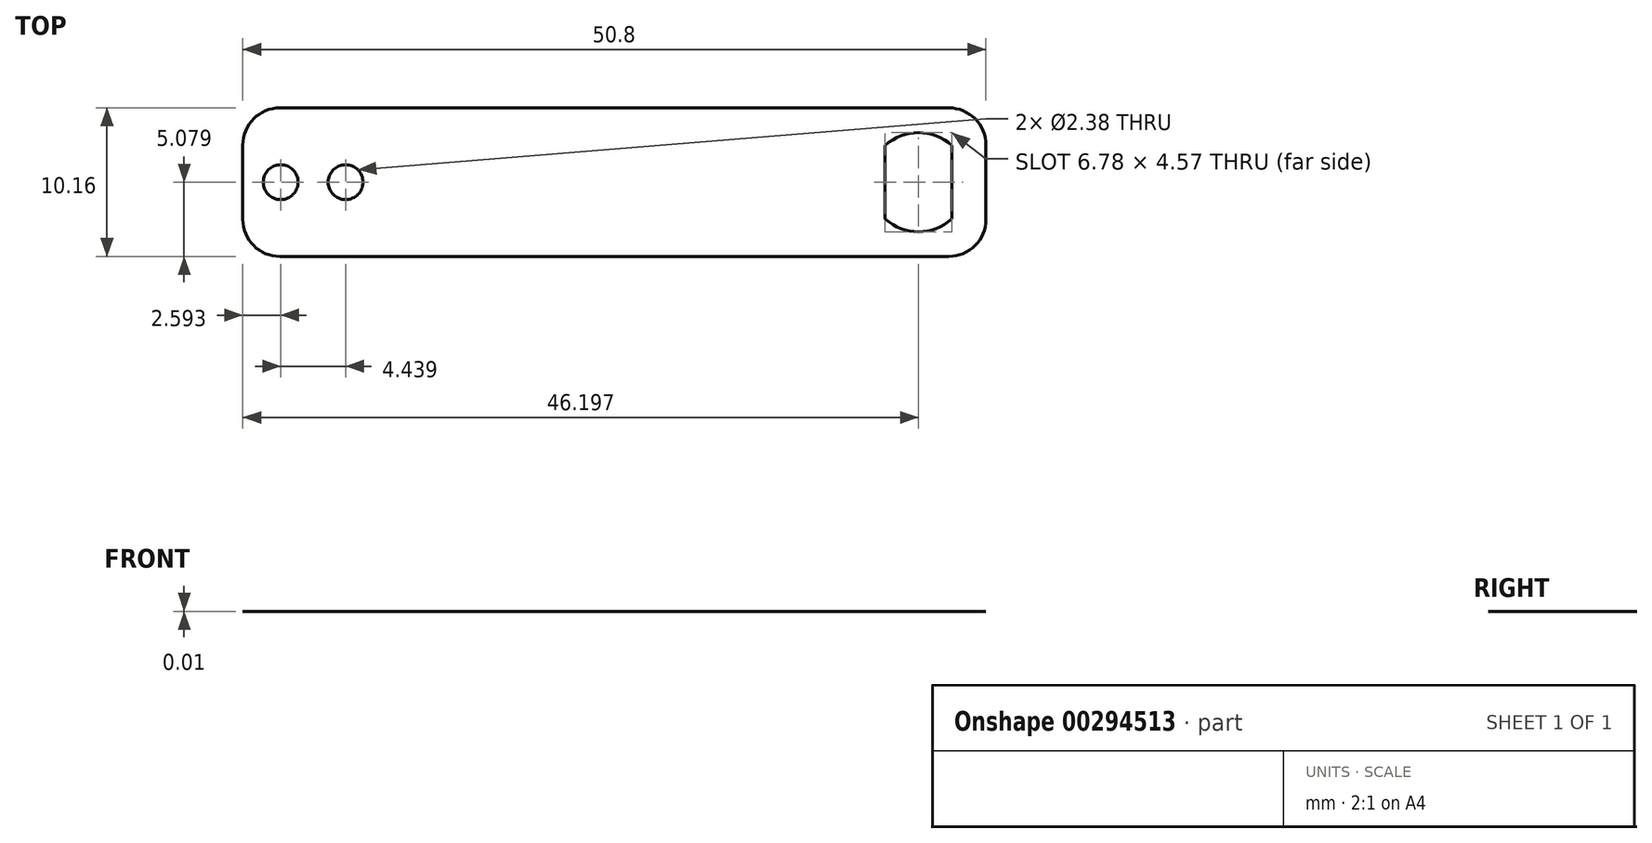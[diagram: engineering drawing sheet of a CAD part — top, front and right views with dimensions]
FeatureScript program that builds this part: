
annotation { "Feature Type Name" : "Feature", "Feature Type Description" : "" }
export const myFeature = defineFeature(function(context is Context, id is Id, definition is map)
    precondition{}
    {
        {
            var Q0;
            Q0=qCreatedBy(makeId("Top.planeOp"),FACE);
            var sketch = newSketch(context, id + "F0", { "sketchPlane" : qUnion([Q0])});
            skLineSegment(sketch, "E0.bottom", {"start": v(23.47, 15.87) * mm, "end": v(-27.33, 15.87) * mm});
            skLineSegment(sketch, "E0.top", {"start": v(23.47, 5.7) * mm, "end": v(-27.33, 5.7) * mm});
            skLineSegment(sketch, "E0.left", {"start": v(23.47, 15.87) * mm, "end": v(23.47, 5.7) * mm});
            skLineSegment(sketch, "E0.right", {"start": v(-27.33, 15.87) * mm, "end": v(-27.33, 5.7) * mm});
            skPoint(sketch, "E0.middle", {"position": v(-1.93, 10.79) * mm});
            skLineSegment(sketch, "E1", {"start": v(-27.33, 10.79) * mm, "end": v(23.47, 10.79) * mm});
            skCircle(sketch, "E2", {"center": v(-24.74, 10.79) * mm, "radius": 1.2 * mm});
            skCircle(sketch, "E3", {"center": v(-20.3, 10.79) * mm, "radius": 1.2 * mm});
            skCircle(sketch, "E4", {"center": v(18.87, 10.79) * mm, "radius": 3.4 * mm});
            skLineSegment(sketch, "E5", {"start": v(16.58, 13.3) * mm, "end": v(16.58, 8.28) * mm});
            skLineSegment(sketch, "E6", {"start": v(21.15, 13.3) * mm, "end": v(21.15, 8.28) * mm});
            skSolve(sketch);
        }
        {
            var Q0;
            {var subQ12=sQuery(id+"F0.wireOp",EDGE,"E0.bottom");Q0=makeQuery(id+"F0.imprint","IMPRINT",FACE,{"disambiguationData":[TD([[makeQuery(id+"F0.imprint","IMPRINT",EDGE,{"derivedFrom":subQ12}),1.0]])]});}
            var Q1;
            {var subQ9=sQuery(id+"F0.wireOp",EDGE,"E0.top");Q1=makeQuery(id+"F0.imprint","IMPRINT",FACE,{"disambiguationData":[TD([[makeQuery(id+"F0.imprint","IMPRINT",EDGE,{"derivedFrom":subQ9}),-1.0]])]});}
            var Q2;
            {var subQ0=sQuery(id+"F0.wireOp",EDGE,"E4");var subQ1=sQuery(id+"F0.wireOp",EDGE,"E1");var subQ2=makeQuery(id+"F0.imprint","INTERSECT",VERTEX,{"disambiguationData":[OD(0.0)],"derivedFrom":[subQ1,subQ0]});Q2=makeQuery(id+"F0.imprint","IMPRINT",FACE,{"disambiguationData":[TD([[makeQuery(id+"F0.imprint","IMPRINT",EDGE,{"disambiguationData":[TD([[subQ2,-1.0]])],"derivedFrom":subQ1}),-1.0]])]});}
            var Q3;
            {var subQ0=sQuery(id+"F0.wireOp",EDGE,"E4");var subQ1=sQuery(id+"F0.wireOp",EDGE,"E1");var subQ2=makeQuery(id+"F0.imprint","INTERSECT",VERTEX,{"disambiguationData":[OD(0.0)],"derivedFrom":[subQ1,subQ0]});Q3=makeQuery(id+"F0.imprint","IMPRINT",FACE,{"disambiguationData":[TD([[makeQuery(id+"F0.imprint","IMPRINT",EDGE,{"disambiguationData":[TD([[subQ2,-1.0]])],"derivedFrom":subQ1}),1.0]])]});}
            var Q4;
            {var subQ0=sQuery(id+"F0.wireOp",EDGE,"E6");var subQ1=sQuery(id+"F0.wireOp",EDGE,"E1");var subQ2=makeQuery(id+"F0.imprint","INTERSECT",VERTEX,{"derivedFrom":[subQ1,subQ0]});Q4=makeQuery(id+"F0.imprint","IMPRINT",FACE,{"disambiguationData":[TD([[makeQuery(id+"F0.imprint","IMPRINT",EDGE,{"disambiguationData":[TD([[subQ2,-1.0]])],"derivedFrom":subQ1}),1.0]])]});}
            var Q5;
            {var subQ0=sQuery(id+"F0.wireOp",EDGE,"E6");var subQ1=sQuery(id+"F0.wireOp",EDGE,"E1");var subQ2=makeQuery(id+"F0.imprint","INTERSECT",VERTEX,{"derivedFrom":[subQ1,subQ0]});Q5=makeQuery(id+"F0.imprint","IMPRINT",FACE,{"disambiguationData":[TD([[makeQuery(id+"F0.imprint","IMPRINT",EDGE,{"disambiguationData":[TD([[subQ2,-1.0]])],"derivedFrom":subQ1}),-1.0]])]});}
            extrude(context, id + "F1", {"entities" : qUnion([Q0, Q1, Q2, Q3, Q4, Q5]), "depth" : 3 / 406.4 * mm});
        }
        {
            var Q0;
            Q0=makeQuery(id+"F1.opExtrude","SWEPT_EDGE",EDGE,{"disambiguationData":[OSD([sQuery(id+"F0.wireOp",EDGE,"E0.bottom"),sQuery(id+"F0.wireOp",EDGE,"E0.left")])]});
            var Q1;
            Q1=makeQuery(id+"F1.opExtrude","SWEPT_EDGE",EDGE,{"disambiguationData":[OSD([sQuery(id+"F0.wireOp",EDGE,"E0.bottom"),sQuery(id+"F0.wireOp",EDGE,"E0.right")])]});
            var Q2;
            Q2=makeQuery(id+"F1.opExtrude","SWEPT_EDGE",EDGE,{"disambiguationData":[OSD([sQuery(id+"F0.wireOp",EDGE,"E0.top"),sQuery(id+"F0.wireOp",EDGE,"E0.right")])]});
            var Q3;
            Q3=makeQuery(id+"F1.opExtrude","SWEPT_EDGE",EDGE,{"disambiguationData":[OSD([sQuery(id+"F0.wireOp",EDGE,"E0.top"),sQuery(id+"F0.wireOp",EDGE,"E0.left")])]});
            fillet(context, id + "F2", {"entities" : qUnion([Q0, Q1, Q2, Q3]), "radius" : 2.54 * mm, "tangentPropagation" : true, "allowEdgeOverflow" : false});
        }
    });
